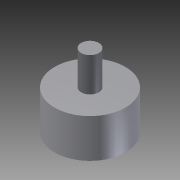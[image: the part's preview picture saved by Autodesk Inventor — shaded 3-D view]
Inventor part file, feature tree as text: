
AUTODESK INVENTOR PART (.ipt)
format: ipt  version: 2012 (Build 160160000, 160)  size: 137,728 bytes
history: native  units: mm
features: extrude x4, sketch x4, other x3, projected_geometry x2, fillet x1
ambient origin geometry x8: Origin, YZ Plane, XZ Plane, XY Plane, X Axis, Y Axis, Z Axis, Center Point
bodies: Solid1 (feature_tree)
feature tree (14):
  other  "ServoToScrewKey.ipt"
  extrude  "Extrusion1"  TaperAngle=0.0deg  [1 undecoded]
  extrude  "Extrusion2"  Depth=20.78461mm
  extrude  "Extrusion3"  Depth=10.0mm TaperAngle=0.0deg
  extrude  "Extrusion5"  Depth=1.0mm
  fillet  "Fillet1"  Radius=4.0mm
  other  "Solid2::ServoToScrewKey.ipt"
  other  "TaggingFeature1"
  sketch  "Sketch2"  dims[d0=10.0mm d1=0.0mm d2=0.0mm]
  projected_geometry  "Projected Loop1"
  sketch  "Sketch3"  dims[d3=12.0mm d4=0.0mm d5=20.78461mm]
  sketch  "Sketch4"  dims[d6=5.196152mm d7=10.0mm d8=0.0mm]
  projected_geometry  "Projected Loop2"
  sketch  "Sketch6"  dims[d20=1.0mm d21=1.0mm d22=4.0mm d23=60.0mm d25=360.0deg d27=10.0mm d28=0.0mm d29=0.5mm]
note: 1 required parameter value undecoded (feature->parameter linkage not recoverable at this tier; creation-order binding heuristic only, values carry confidence <= 0.55)
